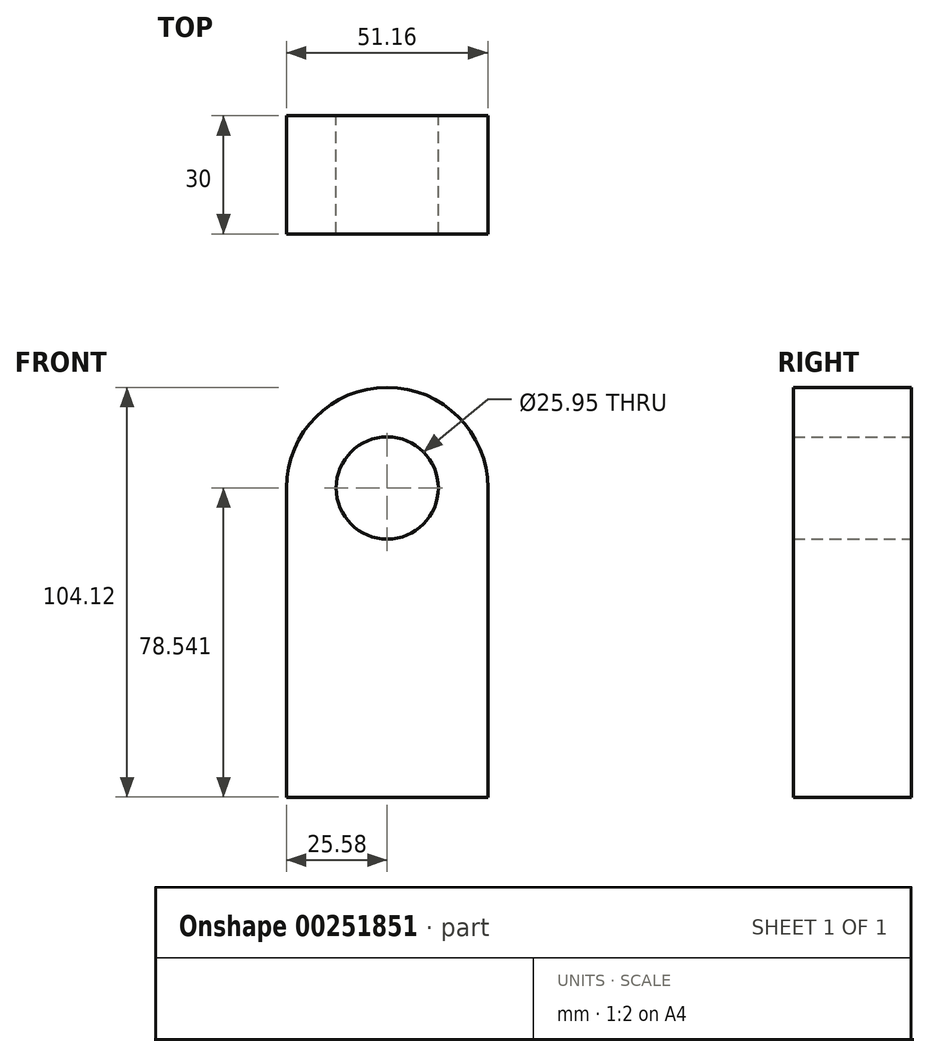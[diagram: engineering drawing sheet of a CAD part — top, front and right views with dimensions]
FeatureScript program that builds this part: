
annotation { "Feature Type Name" : "Feature", "Feature Type Description" : "" }
export const myFeature = defineFeature(function(context is Context, id is Id, definition is map)
    precondition{}
    {
        {
            var Q0;
            Q0=qCreatedBy(makeId("Front.planeOp"),FACE);
            var sketch = newSketch(context, id + "F0", { "sketchPlane" : qUnion([Q0])});
            skLineSegment(sketch, "E0.top", {"start": v(-25.58, -39.27) * mm, "end": v(25.58, -39.27) * mm});
            skLineSegment(sketch, "E0.left", {"start": v(-25.58, 39.27) * mm, "end": v(-25.58, -39.27) * mm});
            skLineSegment(sketch, "E0.right", {"start": v(25.58, 39.27) * mm, "end": v(25.58, -39.27) * mm});
            skPoint(sketch, "E0.middle", {"position": v(0, 0) * mm});
            skArc(sketch, "E1", {"start": v(25.58, 39.27) * mm, "mid": v(0, 64.85) * mm, "end": v(-25.58, 39.27) * mm});
            skCircle(sketch, "E2", {"center": v(0, 39.27) * mm, "radius": 12.98 * mm});
            skSolve(sketch);
        }
        {
            var Q0;
            Q0=makeQuery(id+"F0.imprint","IMPRINT",FACE,{"disambiguationData":[TD([[makeQuery(id+"F0.imprint","IMPRINT",EDGE,{"derivedFrom":sQuery(id+"F0.wireOp",EDGE,"E0.top")}),1.0]])]});
            extrude(context, id + "F1", {"entities" : qUnion([Q0]), "depth" : 30 * mm});
        }
    });
